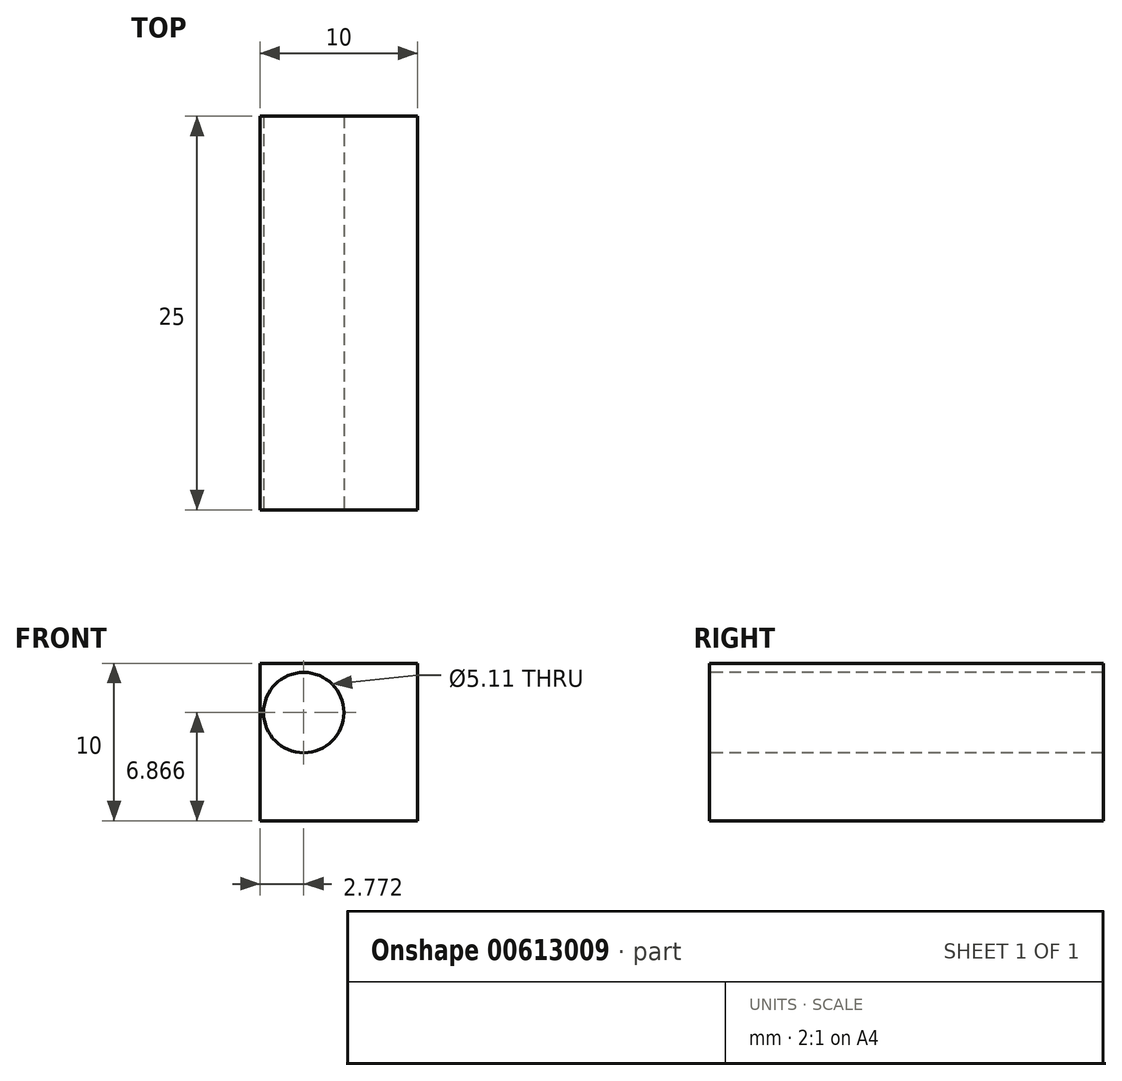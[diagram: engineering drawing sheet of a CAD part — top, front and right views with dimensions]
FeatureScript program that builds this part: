
annotation { "Feature Type Name" : "Feature", "Feature Type Description" : "" }
export const myFeature = defineFeature(function(context is Context, id is Id, definition is map)
    precondition{}
    {
        {
            var Q0;
            Q0=qCreatedBy(makeId("Front.planeOp"),FACE);
            var sketch = newSketch(context, id + "F0", { "sketchPlane" : qUnion([Q0])});
            skLineSegment(sketch, "E0.bottom", {"start": v(-1.65, 9.2) * mm, "end": v(8.35, 9.2) * mm});
            skLineSegment(sketch, "E0.top", {"start": v(-1.65, -0.8) * mm, "end": v(8.35, -0.8) * mm});
            skLineSegment(sketch, "E0.left", {"start": v(-1.65, 9.2) * mm, "end": v(-1.65, -0.8) * mm});
            skLineSegment(sketch, "E0.right", {"start": v(8.35, 9.2) * mm, "end": v(8.35, -0.8) * mm});
            skSolve(sketch);
        }
        {
            var Q0;
            Q0=makeQuery(id+"F0.imprint","IMPRINT",FACE,{"disambiguationData":[TD([[makeQuery(id+"F0.imprint","IMPRINT",EDGE,{"derivedFrom":sQuery(id+"F0.wireOp",EDGE,"E0.bottom")}),-1.0]])]});
            extrude(context, id + "F1", {"entities" : qUnion([Q0]), "oppositeDirection" : true, "depth" : 25 * mm, "offsetDistance" : 25 * mm});
        }
        {
            var Q0;
            Q0=makeQuery(id+"F1.opExtrude","CAP_FACE",FACE,{"disambiguationData":[OSD([sQuery(id+"F0.wireOp",EDGE,"E0.bottom"),sQuery(id+"F0.wireOp",EDGE,"E0.top"),sQuery(id+"F0.wireOp",EDGE,"E0.left"),sQuery(id+"F0.wireOp",EDGE,"E0.right")])],"isStart":true});
            var sketch = newSketch(context, id + "F2", { "sketchPlane" : qUnion([Q0])});
            skCircle(sketch, "E1", {"center": v(1.12, 6.07) * mm, "radius": 2.4 * mm});
            skSolve(sketch);
        }
        {
            var Q0;
            Q0=sQuery(id+"F2.wireOp",VERTEX,"E1.center");
            var Q1;
            Q1=makeQuery(id+"F1.opExtrude","SWEPT_BODY",BODY,{"disambiguationData":[OSD([sQuery(id+"F0.wireOp",EDGE,"E0.bottom"),sQuery(id+"F0.wireOp",EDGE,"E0.top"),sQuery(id+"F0.wireOp",EDGE,"E0.left"),sQuery(id+"F0.wireOp",EDGE,"E0.right")])]});
            hole(context, id + "F3", {"style" : HoleStyle.SIMPLE, "endStyle" : HoleEndStyle.THROUGH, "standardTappedOrClearance" : lookupTablePath({ "standard" : "ANSI", "engagement" : "75%", "pitch" : "20 tpi", "size" : "1/4", "type" : "Tapped" }), "standardBlindInLast" : lookupTablePath({ "standard" : "ANSI", "engagement" : "75%", "pitch" : "20 tpi", "size" : "1/4", "type" : "Tapped" }), "holeDiameter" : 5.1 * mm, "majorDiameter" : 6.35 * mm, "showTappedDepth" : true, "isTappedThrough" : true, "tappedDepth" : 26.2 * mm, "tapClearance" : 3, "locations" : qUnion([Q0]), "scope" : qUnion([Q1])});
        }
    });
